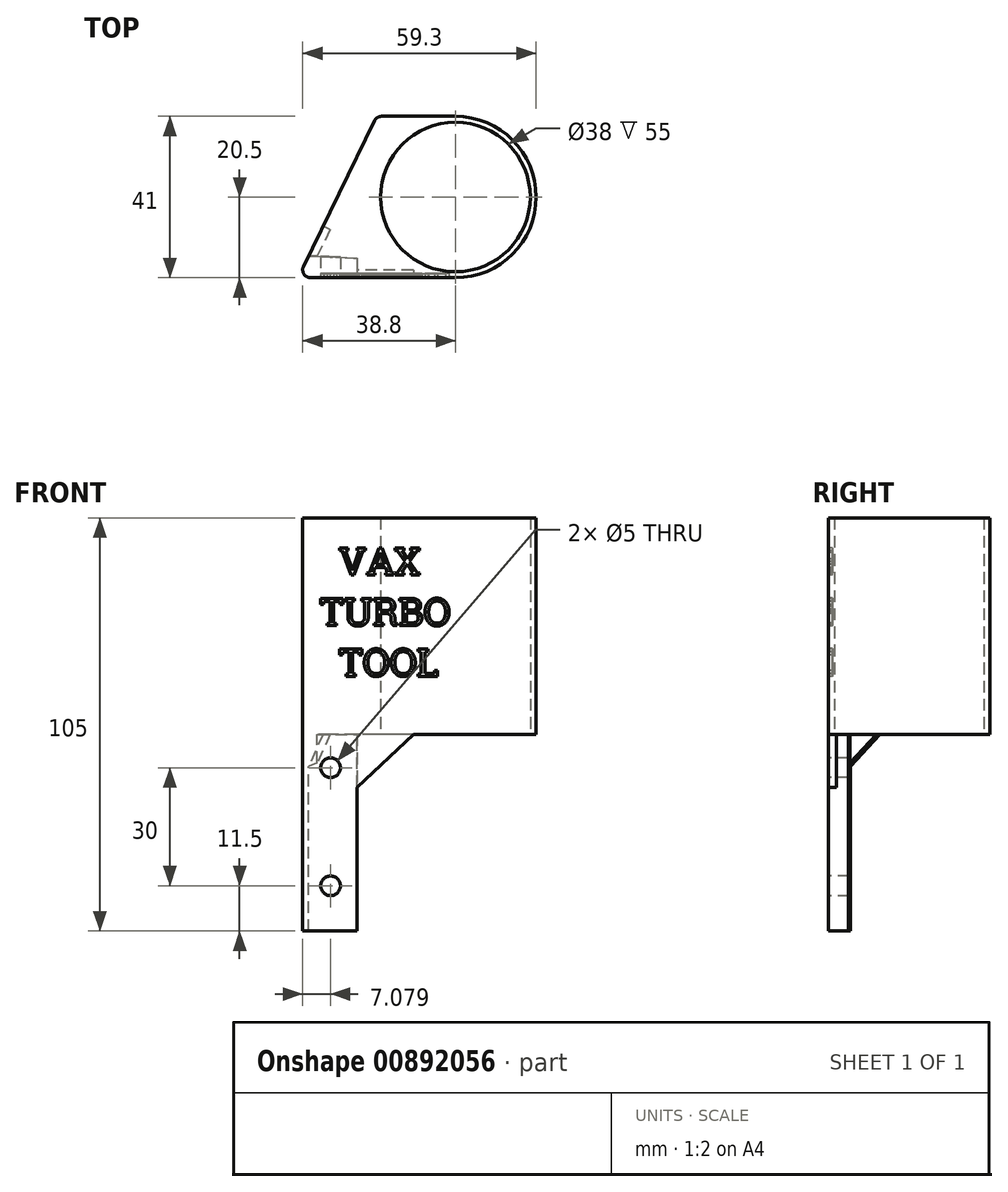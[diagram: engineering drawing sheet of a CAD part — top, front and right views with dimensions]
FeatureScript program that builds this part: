
annotation { "Feature Type Name" : "Feature", "Feature Type Description" : "" }
export const myFeature = defineFeature(function(context is Context, id is Id, definition is map)
    precondition{}
    {
        {
            var Q0;
            Q0=qCreatedBy(makeId("Top.planeOp"),FACE);
            var sketch = newSketch(context, id + "F0", { "sketchPlane" : qUnion([Q0])});
            skCircle(sketch, "E0", {"center": v(0, 0) * mm, "radius": 20.5 * mm});
            skCircle(sketch, "E1", {"center": v(0, 0) * mm, "radius": 19 * mm});
            skLineSegment(sketch, "E2", {"start": v(0, 0) * mm, "end": v(0, 20.5) * mm});
            skLineSegment(sketch, "E3", {"start": v(0, 20.5) * mm, "end": v(-20, 20.5) * mm});
            skLineSegment(sketch, "E4", {"start": v(0, -20.5) * mm, "end": v(-40, -20.5) * mm});
            skLineSegment(sketch, "E5", {"start": v(-20, 20.5) * mm, "end": v(-40, -20.5) * mm});
            skSolve(sketch);
        }
        {
            var Q0;
            Q0=qSketchRegion(id+"F0",true);
            extrude(context, id + "F1", {"entities" : qUnion([Q0]), "depth" : 105 * mm, "offsetDistance" : 25 * mm});
        }
        {
            var Q0;
            {var subQ0=sQuery(id+"F0.wireOp",EDGE,"E3");Q0=makeQuery(id+"F0.imprint","IMPRINT",FACE,{"disambiguationData":[TD([[makeQuery(id+"F0.imprint","IMPRINT",EDGE,{"derivedFrom":subQ0}),1.0]])]});}
            var sketch = newSketch(context, id + "F2", { "sketchPlane" : qUnion([Q0])});
            skLineSegment(sketch, "E6", {"start": v(-92.3, 24.13) * mm, "end": v(-20.7, 24.13) * mm});
            skLineSegment(sketch, "E7", {"start": v(-92.68, -12.5) * mm, "end": v(-92.3, 24.13) * mm});
            skLineSegment(sketch, "E8", {"start": v(-25, -15.5) * mm, "end": v(-25, -22) * mm});
            skLineSegment(sketch, "E9", {"start": v(-25, -22) * mm, "end": v(-20.75, -22) * mm});
            skLineSegment(sketch, "E10", {"start": v(-20.7, 24.13) * mm, "end": v(-20.75, -22) * mm});
            skLineSegment(sketch, "E11", {"start": v(-92.68, -12.5) * mm, "end": v(-25, -15.5) * mm});
            skSolve(sketch);
        }
        {
            var Q0;
            Q0=qSketchRegion(id+"F2",true);
            extrude(context, id + "F3", {"entities" : qUnion([Q0]), "operationType" : NewBodyOperationType.REMOVE, "depth" : 50 * mm, "offsetDistance" : 25 * mm});
        }
        {
            var Q0;
            {var subQ0=sQuery(id+"F2.wireOp",EDGE,"E10");var subQ1=sQuery(id+"F0.wireOp",EDGE,"E3");var subQ2=makeQuery(id+"F0.imprint","IMPRINT",EDGE,{"derivedFrom":subQ1});var subQ3=makeQuery(id+"F2.imprint","INTERSECT",VERTEX,{"derivedFrom":[subQ2,subQ0]});Q0=makeQuery(id+"F2.imprint","IMPRINT",FACE,{"disambiguationData":[TD([[makeQuery(id+"F2.imprint","IMPRINT",EDGE,{"disambiguationData":[TD([[subQ3,-1.0]])],"derivedFrom":subQ0}),1.0]])]});}
            var sketch = newSketch(context, id + "F4", { "sketchPlane" : qUnion([Q0])});
            skLineSegment(sketch, "E12.bottom", {"start": v(-24.09, -27.18) * mm, "end": v(22.58, -27.18) * mm});
            skLineSegment(sketch, "E12.top", {"start": v(-24.09, 30.66) * mm, "end": v(22.58, 30.66) * mm});
            skLineSegment(sketch, "E12.left", {"start": v(-24.09, -27.18) * mm, "end": v(-24.09, 30.66) * mm});
            skLineSegment(sketch, "E12.right", {"start": v(22.58, -27.18) * mm, "end": v(22.58, 30.66) * mm});
            skSolve(sketch);
        }
        {
            var Q0;
            Q0=qSketchRegion(id+"F4",true);
            extrude(context, id + "F5", {"entities" : qUnion([Q0]), "operationType" : NewBodyOperationType.REMOVE, "depth" : 50 * mm, "offsetDistance" : 25 * mm});
        }
        {
            var Q0;
            Q0=makeQuery(id+"F1.opExtrude","SWEPT_FACE",FACE,{"disambiguationData":[OSD([sQuery(id+"F0.wireOp",EDGE,"E4")])]});
            var sketch = newSketch(context, id + "F6", { "sketchPlane" : qUnion([Q0])});
            skPoint(sketch, "E13", {"position": v(-31.72, 41.5) * mm});
            skPoint(sketch, "E14", {"position": v(-31.72, 11.5) * mm});
            skSolve(sketch);
        }
        {
            var Q0;
            Q0=makeQuery(id+"F1.opExtrude","SWEPT_FACE",FACE,{"disambiguationData":[OSD([sQuery(id+"F0.wireOp",EDGE,"E5")])]});
            var sketch = newSketch(context, id + "F7", { "sketchPlane" : qUnion([Q0])});
            skLineSegment(sketch, "E15", {"start": v(15.92, 55.35) * mm, "end": v(32.14, 39.57) * mm});
            skLineSegment(sketch, "E16", {"start": v(32.14, 39.57) * mm, "end": v(32.14, 43.17) * mm});
            skLineSegment(sketch, "E17", {"start": v(32.14, 43.17) * mm, "end": v(32.14, 55.3) * mm});
            skLineSegment(sketch, "E18", {"start": v(32.14, 55.3) * mm, "end": v(15.92, 55.35) * mm});
            skSolve(sketch);
        }
        {
            var Q0;
            {var subQ0=sQuery(id+"F7.wireOp",EDGE,"E15");var subQ1=sQuery(id+"F2.wireOp",EDGE,"E11");var subQ2=makeQuery(id+"F1.opExtrude","SWEPT_FACE",FACE,{"disambiguationData":[OSD([sQuery(id+"F0.wireOp",EDGE,"E5")])]});var subQ5=makeQuery(id+"F3.boolean.opBoolean","INTERSECT",EDGE,{"derivedFrom":[subQ2,makeQuery(id+"F3.opExtrude","SWEPT_FACE",FACE,{"disambiguationData":[OSD([subQ1])]})]});var subQ6=makeQuery(id+"F7.imprint","INTERSECT",VERTEX,{"derivedFrom":[subQ5,subQ0]});Q0=makeQuery(id+"F7.imprint","IMPRINT",FACE,{"disambiguationData":[TD([[makeQuery(id+"F7.imprint","IMPRINT",EDGE,{"disambiguationData":[TD([[subQ6,1.0]])],"derivedFrom":subQ0}),1.0]])]});}
            var Q1;
            Q1=makeQuery(id+"F1.opExtrude","SWEPT_FACE",FACE,{"disambiguationData":[OSD([sQuery(id+"F0.wireOp",EDGE,"E4")])]});
            extrude(context, id + "F8", {"entities" : qUnion([Q0]), "operationType" : NewBodyOperationType.ADD, "oppositeDirection" : true, "depth" : 2 * mm, "endBoundEntityFace" : qUnion([Q1]), "offsetDistance" : 25 * mm});
        }
        {
            var Q0;
            Q0=sQuery(id+"F6.wireOp",VERTEX,"E13");
            var Q1;
            Q1=sQuery(id+"F6.wireOp",VERTEX,"E14");
            var Q2;
            Q2=makeQuery(id+"F1.opExtrude","SWEPT_BODY",BODY,{"disambiguationData":[OSD([sQuery(id+"F0.wireOp",EDGE,"E0"),sQuery(id+"F0.wireOp",EDGE,"E1"),sQuery(id+"F0.wireOp",EDGE,"E3"),sQuery(id+"F0.wireOp",EDGE,"E4"),sQuery(id+"F0.wireOp",EDGE,"E5")])]});
            hole(context, id + "F9", {"style" : HoleStyle.SIMPLE, "endStyle" : HoleEndStyle.THROUGH, "holeDiameter" : 5 * mm, "majorDiameter" : 5 * mm, "isTappedThrough" : true, "tappedDepth" : 12 * mm, "tapClearance" : 3, "locations" : qUnion([Q0, Q1]), "scope" : qUnion([Q2])});
        }
        {
            var Q0;
            Q0=makeQuery(id+"F1.opExtrude","SWEPT_EDGE",EDGE,{"disambiguationData":[OSD([sQuery(id+"F0.wireOp",EDGE,"E3"),sQuery(id+"F0.wireOp",EDGE,"E5")])]});
            var Q1;
            Q1=makeQuery(id+"F1.opExtrude","SWEPT_EDGE",EDGE,{"disambiguationData":[OSD([sQuery(id+"F0.wireOp",EDGE,"E4"),sQuery(id+"F0.wireOp",EDGE,"E5")])]});
            fillet(context, id + "F10", {"entities" : qUnion([Q0, Q1]), "radius" : 2 * mm, "tangentPropagation" : true, "allowEdgeOverflow" : false});
        }
        {
            var Q0;
            Q0=makeQuery(id+"F1.opExtrude","SWEPT_FACE",FACE,{"disambiguationData":[OSD([sQuery(id+"F0.wireOp",EDGE,"E4")])]});
            var sketch = newSketch(context, id + "F11", { "sketchPlane" : qUnion([Q0])});
            skLineSegment(sketch, "E19", {"start": v(-25, 36.56) * mm, "end": v(-6.02, 54.4) * mm});
            skLineSegment(sketch, "E20", {"start": v(-6.02, 54.4) * mm, "end": v(-27.51, 54.4) * mm});
            skLineSegment(sketch, "E21", {"start": v(-27.51, 54.4) * mm, "end": v(-27.51, 33.87) * mm});
            skLineSegment(sketch, "E22", {"start": v(-27.51, 33.87) * mm, "end": v(-25, 36.56) * mm});
            skSolve(sketch);
        }
        {
            var Q0;
            {var subQ0=sQuery(id+"F11.wireOp",EDGE,"E19");var subQ1=makeQuery(id+"F1.opExtrude","SWEPT_FACE",FACE,{"disambiguationData":[OSD([sQuery(id+"F0.wireOp",EDGE,"E4")])]});var subQ2=makeQuery(id+"F3.boolean.opBoolean","INTERSECT",EDGE,{"derivedFrom":[subQ1,makeQuery(id+"F3.opExtrude","SWEPT_FACE",FACE,{"disambiguationData":[OSD([sQuery(id+"F2.wireOp",EDGE,"E8")])]})]});var subQ3=makeQuery(id+"F11.imprint","INTERSECT",VERTEX,{"derivedFrom":[subQ2,subQ0,sQuery(id+"F11.wireOp",EDGE,"E22")]});Q0=makeQuery(id+"F11.imprint","IMPRINT",FACE,{"disambiguationData":[TD([[makeQuery(id+"F11.imprint","IMPRINT",EDGE,{"disambiguationData":[TD([[subQ3,-1.0]])],"derivedFrom":subQ0}),1.0]])]});}
            extrude(context, id + "F12", {"entities" : qUnion([Q0]), "operationType" : NewBodyOperationType.ADD, "oppositeDirection" : true, "depth" : 2 * mm, "offsetDistance" : 25 * mm});
        }
        {
            var Q0;
            {var subQ0=sQuery(id+"F0.wireOp",EDGE,"E4");Q0=makeQuery(id+"F12.boolean.opBoolean","MERGE",FACE,{"derivedFrom":[makeQuery(id+"F1.opExtrude","SWEPT_FACE",FACE,{"disambiguationData":[OSD([subQ0])]}),makeQuery(id+"F12.opExtrude","CAP_FACE",FACE,{"disambiguationData":[OSD([subQ0,sQuery(id+"F2.wireOp",EDGE,"E8"),sQuery(id+"F4.wireOp",EDGE,"E12.bottom"),sQuery(id+"F4.wireOp",EDGE,"E12.top"),sQuery(id+"F4.wireOp",EDGE,"E12.left"),sQuery(id+"F4.wireOp",EDGE,"E12.right"),sQuery(id+"F11.wireOp",EDGE,"E19")])],"isStart":true})]});}
            var sketch = newSketch(context, id + "F13", { "sketchPlane" : qUnion([Q0])});
            skText(sketch, "E23", { "text": "  VAX\nTURBO\n  TOOL", "fontName": "RobotoSlab-Regular.ttf"});
            const initialGuessF13  = {"E23": [-0.03448, 0.09042, 1, 0, 0.007]};
            skSetInitialGuess(sketch, initialGuessF13);
            skSolve(sketch);
        }
        {
            var Q0;
            Q0 = qSketchRegion(id + "F13", true);
            extrude(context, id + "F14", {"entities" : qUnion([Q0]), "operationType" : NewBodyOperationType.REMOVE, "oppositeDirection" : true, "depth" : 1 * mm, "offsetDistance" : 25 * mm});
        }
    });
